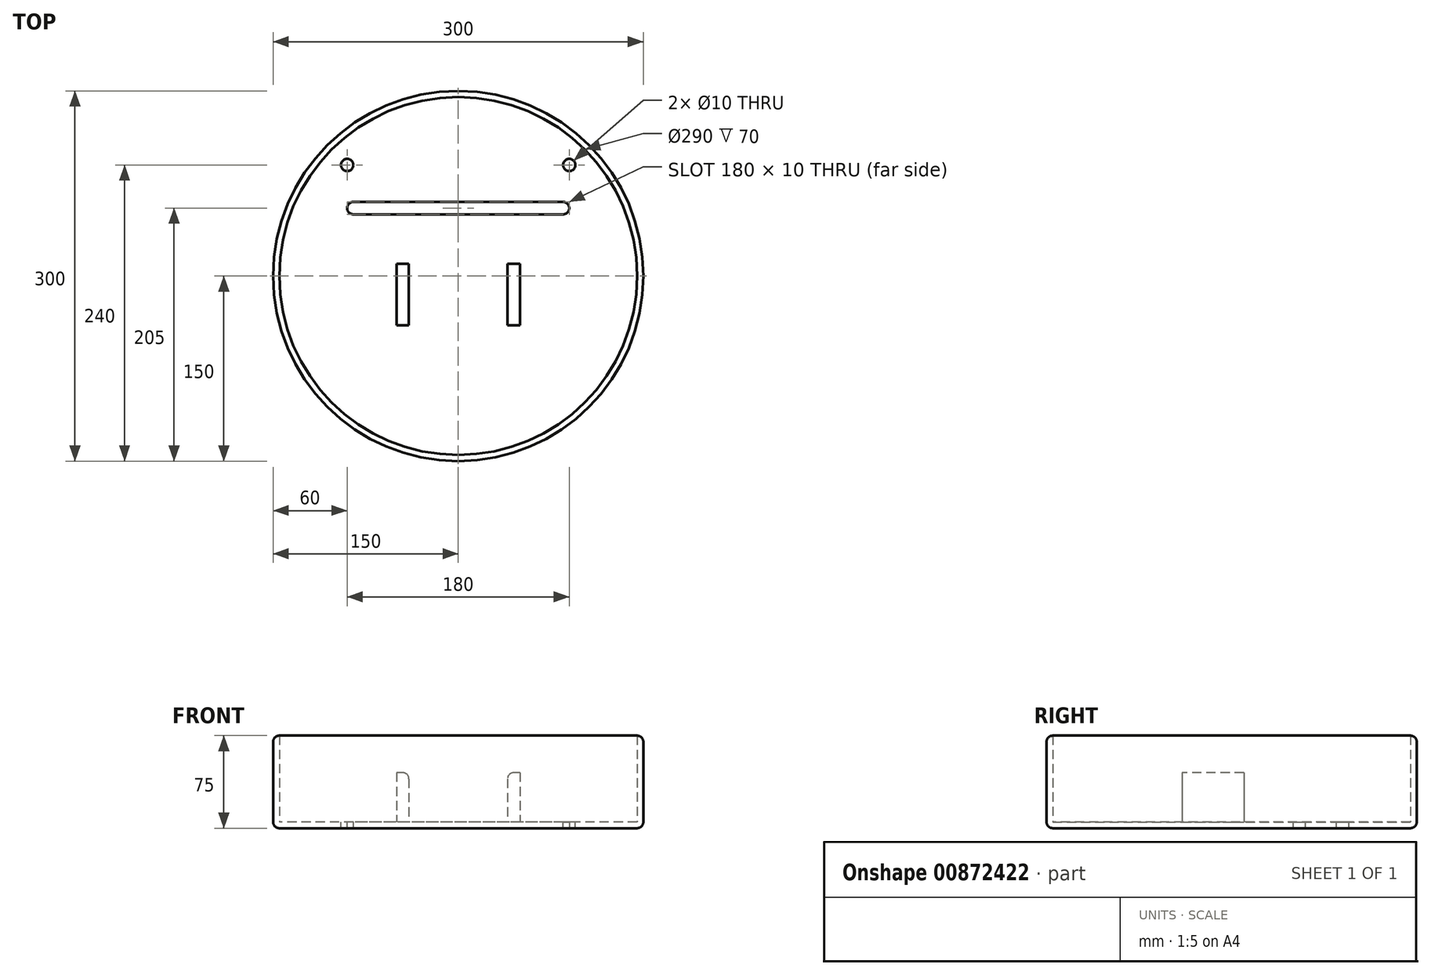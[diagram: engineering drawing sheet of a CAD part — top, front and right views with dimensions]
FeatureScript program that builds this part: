
annotation { "Feature Type Name" : "Feature", "Feature Type Description" : "" }
export const myFeature = defineFeature(function(context is Context, id is Id, definition is map)
    precondition{}
    {
        {
            var Q0;
            Q0=qCreatedBy(makeId("Top.planeOp"),FACE);
            var sketch = newSketch(context, id + "F0", { "sketchPlane" : qUnion([Q0])});
            skCircle(sketch, "E0", {"center": v(0, 0) * mm, "radius": 150 * mm});
            skSolve(sketch);
        }
        {
            var Q0;
            Q0=makeQuery(id+"F0.imprint","IMPRINT",FACE,{"disambiguationData":[TD([[makeQuery(id+"F0.imprint","IMPRINT",EDGE,{"derivedFrom":sQuery(id+"F0.wireOp",EDGE,"E0")}),1.0]])]});
            extrude(context, id + "F1", {"entities" : qUnion([Q0]), "depth" : 5 * mm, "offsetDistance" : 25 * mm});
        }
        {
            var Q0;
            Q0=makeQuery(id+"F1.opExtrude","CAP_FACE",FACE,{"disambiguationData":[OSD([sQuery(id+"F0.wireOp",EDGE,"E0")])],"isStart":false});
            var sketch = newSketch(context, id + "F2", { "sketchPlane" : qUnion([Q0])});
            skCircle(sketch, "E1", {"center": v(0, 0) * mm, "radius": 150 * mm});
            skCircle(sketch, "E2", {"center": v(0, 0) * mm, "radius": 145 * mm});
            skSolve(sketch);
        }
        {
            var Q0;
            Q0=makeQuery(id+"F2.imprint","IMPRINT",FACE,{"disambiguationData":[TD([[makeQuery(id+"F2.imprint","IMPRINT",EDGE,{"derivedFrom":sQuery(id+"F2.wireOp",EDGE,"E1")}),1.0]])]});
            extrude(context, id + "F3", {"entities" : qUnion([Q0]), "operationType" : NewBodyOperationType.ADD, "depth" : 70 * mm, "offsetDistance" : 25 * mm});
        }
        {
            var Q0;
            Q0=makeQuery(id+"F3.opExtrude","CAP_EDGE",EDGE,{"disambiguationData":[OSD([sQuery(id+"F2.wireOp",EDGE,"E1")])],"isStart":false});
            fillet(context, id + "F4", {"entities" : qUnion([Q0]), "radius" : 5 * mm, "tangentPropagation" : true, "allowEdgeOverflow" : false});
        }
        {
            var Q0;
            Q0=makeQuery(id+"F1.opExtrude","CAP_EDGE",EDGE,{"disambiguationData":[OSD([sQuery(id+"F0.wireOp",EDGE,"E0")])],"isStart":true});
            fillet(context, id + "F5", {"entities" : qUnion([Q0]), "radius" : 5 * mm, "tangentPropagation" : true, "allowEdgeOverflow" : false});
        }
        {
            var Q0;
            Q0=makeQuery(id+"F1.opExtrude","CAP_FACE",FACE,{"disambiguationData":[OSD([sQuery(id+"F0.wireOp",EDGE,"E0")])],"isStart":false});
            var sketch = newSketch(context, id + "F6", { "sketchPlane" : qUnion([Q0])});
            skLineSegment(sketch, "E3", {"start": v(0, 0) * mm, "end": v(0, 90) * mm});
            skLineSegment(sketch, "E4", {"start": v(0, 90) * mm, "end": v(90, 90) * mm});
            skLineSegment(sketch, "E5", {"start": v(0, 90) * mm, "end": v(-90, 90) * mm});
            skCircle(sketch, "E6", {"center": v(-90, 90) * mm, "radius": 5 * mm});
            skCircle(sketch, "E7", {"center": v(90, 90) * mm, "radius": 5 * mm});
            skSolve(sketch);
        }
        {
            var Q0;
            Q0=makeQuery(id+"F6.imprint","IMPRINT",FACE,{"disambiguationData":[TD([[makeQuery(id+"F6.imprint","IMPRINT",EDGE,{"derivedFrom":sQuery(id+"F6.wireOp",EDGE,"E6")}),1.0]])]});
            extrude(context, id + "F7", {"entities" : qUnion([Q0]), "operationType" : NewBodyOperationType.REMOVE, "oppositeDirection" : true, "depth" : 10 * mm, "offsetDistance" : 25 * mm});
        }
        {
            var Q0;
            Q0=makeQuery(id+"F6.imprint","IMPRINT",FACE,{"disambiguationData":[TD([[makeQuery(id+"F6.imprint","IMPRINT",EDGE,{"derivedFrom":sQuery(id+"F6.wireOp",EDGE,"E7")}),1.0]])]});
            extrude(context, id + "F8", {"entities" : qUnion([Q0]), "operationType" : NewBodyOperationType.REMOVE, "oppositeDirection" : true, "depth" : 10 * mm, "offsetDistance" : 25 * mm});
        }
        {
            var Q0;
            Q0=makeQuery(id+"F1.opExtrude","CAP_FACE",FACE,{"disambiguationData":[OSD([sQuery(id+"F0.wireOp",EDGE,"E0")])],"isStart":false});
            var sketch = newSketch(context, id + "F9", { "sketchPlane" : qUnion([Q0])});
            skLineSegment(sketch, "E8", {"start": v(0, 0) * mm, "end": v(0, 40) * mm});
            skLineSegment(sketch, "E9", {"start": v(0, 40) * mm, "end": v(0, 50) * mm});
            skLineSegment(sketch, "E10", {"start": v(0, 50) * mm, "end": v(90, 50) * mm});
            skLineSegment(sketch, "E11", {"start": v(0, 50) * mm, "end": v(-90, 50) * mm});
            skLineSegment(sketch, "E12", {"start": v(-90, 50) * mm, "end": v(-90, 60) * mm});
            skLineSegment(sketch, "E13", {"start": v(90, 60) * mm, "end": v(90, 50) * mm});
            skLineSegment(sketch, "E14", {"start": v(90, 60) * mm, "end": v(-90, 60) * mm});
            skSolve(sketch);
        }
        {
            var Q0;
            Q0=makeQuery(id+"F9.imprint","IMPRINT",FACE,{"disambiguationData":[TD([[makeQuery(id+"F9.imprint","IMPRINT",EDGE,{"derivedFrom":sQuery(id+"F9.wireOp",EDGE,"E10")}),1.0]])]});
            extrude(context, id + "F10", {"entities" : qUnion([Q0]), "operationType" : NewBodyOperationType.REMOVE, "oppositeDirection" : true, "depth" : 10 * mm, "offsetDistance" : 25 * mm});
        }
        {
            var Q0;
            Q0=makeQuery(id+"F10.boolean.opBoolean","COPY",EDGE,{"derivedFrom":makeQuery(id+"F10.opExtrude","SWEPT_EDGE",EDGE,{"disambiguationData":[OSD([sQuery(id+"F9.wireOp",EDGE,"E12"),sQuery(id+"F9.wireOp",EDGE,"E14")])]})});
            var Q1;
            Q1=makeQuery(id+"F10.boolean.opBoolean","COPY",EDGE,{"derivedFrom":makeQuery(id+"F10.opExtrude","SWEPT_EDGE",EDGE,{"disambiguationData":[OSD([sQuery(id+"F9.wireOp",EDGE,"E11"),sQuery(id+"F9.wireOp",EDGE,"E12")])]})});
            var Q2;
            Q2=makeQuery(id+"F10.boolean.opBoolean","COPY",EDGE,{"derivedFrom":makeQuery(id+"F10.opExtrude","SWEPT_EDGE",EDGE,{"disambiguationData":[OSD([sQuery(id+"F9.wireOp",EDGE,"E10"),sQuery(id+"F9.wireOp",EDGE,"E13")])]})});
            var Q3;
            Q3=makeQuery(id+"F10.boolean.opBoolean","COPY",EDGE,{"derivedFrom":makeQuery(id+"F10.opExtrude","SWEPT_EDGE",EDGE,{"disambiguationData":[OSD([sQuery(id+"F9.wireOp",EDGE,"E13"),sQuery(id+"F9.wireOp",EDGE,"E14")])]})});
            fillet(context, id + "F11", {"entities" : qUnion([Q0, Q1, Q2, Q3]), "radius" : 5 * mm, "tangentPropagation" : true, "allowEdgeOverflow" : false});
        }
        {
            var Q0;
            Q0=makeQuery(id+"F1.opExtrude","CAP_FACE",FACE,{"disambiguationData":[OSD([sQuery(id+"F0.wireOp",EDGE,"E0")])],"isStart":false});
            var sketch = newSketch(context, id + "F12", { "sketchPlane" : qUnion([Q0])});
            skLineSegment(sketch, "E15", {"start": v(0, 0) * mm, "end": v(-40, 0) * mm});
            skLineSegment(sketch, "E16", {"start": v(0, 0) * mm, "end": v(40, 0) * mm});
            skLineSegment(sketch, "E17", {"start": v(40, 0) * mm, "end": v(40, 10) * mm});
            skLineSegment(sketch, "E18", {"start": v(50, 10) * mm, "end": v(40, 10) * mm});
            skLineSegment(sketch, "E19", {"start": v(50, 10) * mm, "end": v(50, -40) * mm});
            skLineSegment(sketch, "E20", {"start": v(50, -40) * mm, "end": v(40, -40) * mm});
            skLineSegment(sketch, "E21", {"start": v(40, -40) * mm, "end": v(40, 0) * mm});
            skLineSegment(sketch, "E22", {"start": v(-40, 0) * mm, "end": v(-40, 10) * mm});
            skLineSegment(sketch, "E23", {"start": v(-40, 10) * mm, "end": v(-50, 10) * mm});
            skLineSegment(sketch, "E24", {"start": v(-50, 10) * mm, "end": v(-50, -40) * mm});
            skLineSegment(sketch, "E25", {"start": v(-50, -40) * mm, "end": v(-40, -40) * mm});
            skLineSegment(sketch, "E26", {"start": v(-40, -40) * mm, "end": v(-40, 0) * mm});
            skSolve(sketch);
        }
        {
            var Q0;
            Q0=makeQuery(id+"F12.imprint","IMPRINT",FACE,{"disambiguationData":[TD([[makeQuery(id+"F12.imprint","IMPRINT",EDGE,{"derivedFrom":sQuery(id+"F12.wireOp",EDGE,"E17")}),-1.0]])]});
            var Q1;
            Q1=makeQuery(id+"F12.imprint","IMPRINT",FACE,{"disambiguationData":[TD([[makeQuery(id+"F12.imprint","IMPRINT",EDGE,{"derivedFrom":sQuery(id+"F12.wireOp",EDGE,"E22")}),1.0]])]});
            extrude(context, id + "F13", {"entities" : qUnion([Q0, Q1]), "operationType" : NewBodyOperationType.ADD, "depth" : 40 * mm, "offsetDistance" : 25 * mm});
        }
        {
            var Q0;
            Q0=makeQuery(id+"F13.opExtrude","CAP_EDGE",EDGE,{"disambiguationData":[OSD([sQuery(id+"F12.wireOp",EDGE,"E22"),sQuery(id+"F12.wireOp",EDGE,"E26")])],"isStart":false});
            var Q1;
            Q1=makeQuery(id+"F13.opExtrude","CAP_EDGE",EDGE,{"disambiguationData":[OSD([sQuery(id+"F12.wireOp",EDGE,"E17"),sQuery(id+"F12.wireOp",EDGE,"E21")])],"isStart":false});
            fillet(context, id + "F14", {"entities" : qUnion([Q0, Q1]), "radius" : 5 * mm, "tangentPropagation" : true, "allowEdgeOverflow" : false});
        }
    });
